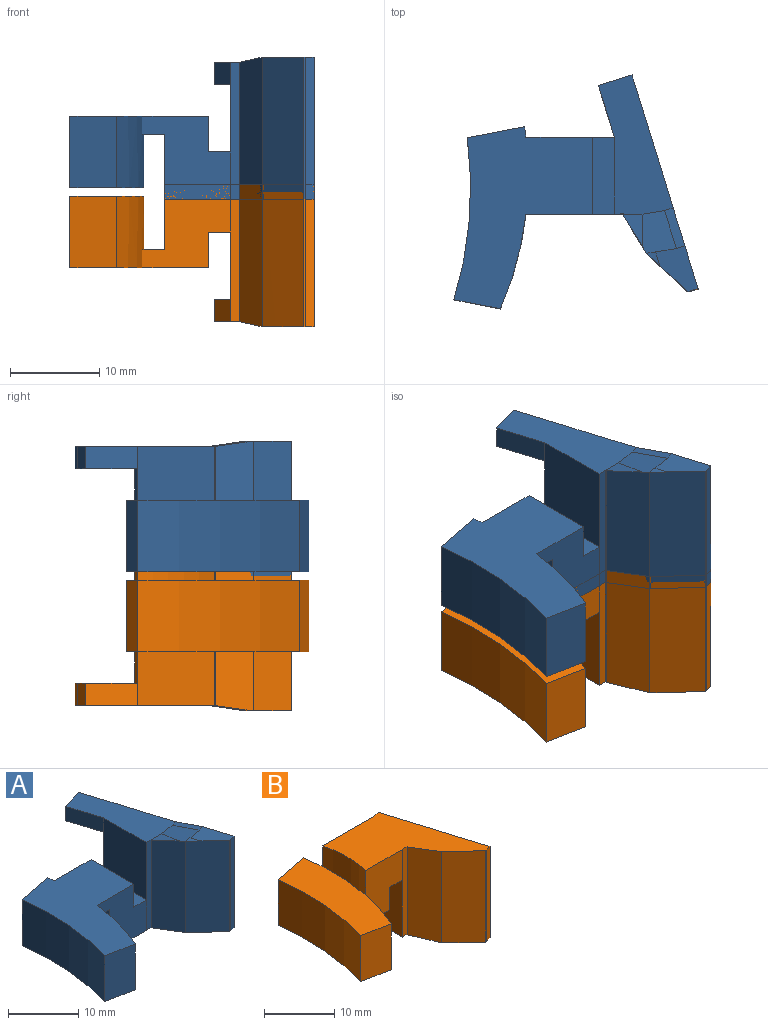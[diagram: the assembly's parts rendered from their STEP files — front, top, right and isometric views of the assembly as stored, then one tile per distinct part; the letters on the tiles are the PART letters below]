
ASSEMBLY  parts=2 mates=1
PART A: 36 faces, bbox 27.3x26.1x15.9 mm
  f0: plane 15.92x4.24mm, normal (0.96,0.3,0), area 69.4mm2, adj f4,f20,f29,f30
  f1: plane 15.32x0.16mm, normal (-0.99,0.14,0), area 2.5mm2, adj f6,f20,f24,f27,f33
  f2: plane 15.92x0mm, normal (-0.96,-0.29,0), area 0mm2, adj f6,f7,f20
  f3: plane 15.92x0.2mm, normal (0.16,-0.99,0), area 3.2mm2, adj f5,f7,f20,f35
  f4: plane 15.92x4.78mm, normal (0.96,0.29,0), area 79.6mm2, adj f0,f5,f20,f35
  f5: plane 15.92x0.96mm, normal (0.29,-0.96,0), area 15.9mm2, adj f3,f4,f20,f35
  f6: plane 15.92x4.25mm, normal (-0.85,-0.52,0), area 77.8mm2, adj f1,f2,f20,f26,f27
  f7: plane 15.92x4.6mm, normal (-0.68,-0.73,0), area 99.9mm2, adj f2,f3,f20,f34,f35
  f8: plane 5.81x2.5mm, normal (-0.96,-0.3,0), area 15.2mm2, adj f22,f24,f25,f32
  f9: plane 6.67x2.5mm, normal (0.96,0.3,0), area 17.5mm2, adj f24,f25,f29,f31
  f10: plane 9.9x9.3mm, normal (0,-1,0), area 63.8mm2, adj f11,f15,f18,f19,f20,f21,f23,f33
  f11: plane 20.36x15.45mm, normal (0,0,1), area 181.4mm2, adj f10,f12,f13,f14,f15,f16,f21
  f12: plane 12.97x12.8mm, normal (0,1,0), area 103.1mm2, adj f11,f15,f18,f19,f20,f21,f22,f23
  f13: cylinder r=42.23mm len=18.11mm, axis (0,0,-1), area 146.5mm2, adj f11,f14,f16,f17
  f14: plane 8x5.2mm, normal (-0.19,-0.98,0), area 42.4mm2, adj f11,f13,f15,f17
  f15: cylinder r=37.1mm len=20.36mm, axis (0,0,-1), area 149.3mm2, adj f10,f11,f12,f14,f16,f17,f18
  f16: plane 8x6.4mm, normal (-0.19,0.98,0), area 52.2mm2, adj f11,f13,f15,f17
  f17: plane 20.36x8.31mm, normal (0,0,-1), area 119.3mm2, adj f13,f14,f15,f16
  f18: plane 8.6x3.05mm, normal (0,0,-1), area 23.2mm2, adj f10,f12,f15,f19
  f19: cylinder r=17.21mm len=8.6mm, axis (0,0,1), area 63.5mm2, adj f10,f12,f18,f20
  f20: plane 17.54x16.74mm, normal (0,0,-1), area 142.3mm2, adj f0,f1,f2,f3,f4,f5,f6,f7
  f21: plane 8.6x4mm, normal (1,0,0), area 34.4mm2, adj f10,f11,f12,f23
  f22: plane 10x8.6mm, normal (-1,0,0), area 86mm2, adj f8,f12,f23,f24,f33
  f23: plane 8.6x2.5mm, normal (0,0,1), area 21.5mm2, adj f10,f12,f21,f22
  f24: plane 15.57x8.35mm, normal (0,0,1), area 72mm2, adj f1,f8,f9,f22,f26,f27,f29,f30
  f25: plane 6.97x5.83mm, normal (0,0,-1), area 26.2mm2, adj f8,f9,f12,f28,f31,f32
  f26: plane 4.79x3.85mm, normal (-0.02,0.14,0.99), area 14mm2, adj f6,f24,f27,f30,f34,f35
  f27: plane 3.66x2.17mm, normal (0,0.14,0.99), area 4mm2, adj f1,f6,f24,f26
  f28: plane 12.8x0.96mm, normal (-0.29,0.96,0), area 12.8mm2, adj f12,f20,f25,f29
  f29: plane 15.3x8.19mm, normal (0.96,0.29,0), area 131.1mm2, adj f0,f9,f20,f24,f28
  f30: plane 4.54x2.27mm, normal (-0.04,0.13,0.99), area 4.5mm2, adj f0,f24,f26,f35
  f31: plane 2.5x0.96mm, normal (-0.29,0.96,0), area 2.5mm2, adj f9,f24,f25,f32
  f32: plane 2.81x2.5mm, normal (-0.3,0.96,0), area 7.3mm2, adj f8,f24,f25,f31
  f33: plane 15.3x1.02mm, normal (0.03,-1,0), area 15.5mm2, adj f1,f10,f20,f22,f24
  f34: plane 1.53x1.47mm, normal (0,0,1), area 0.8mm2, adj f7,f26,f35
  f35: plane 5.1x4.75mm, normal (0,0,1), area 13mm2, adj f3,f4,f5,f7,f26,f30,f34
PART B: 36 faces, bbox 27.3x26.1x15.9 mm
  f0: plane 15.92x4.24mm, normal (0.96,0.3,0), area 69.4mm2, adj f4,f20,f29,f30
  f1: plane 15.32x0.16mm, normal (-0.99,0.14,0), area 2.5mm2, adj f6,f20,f24,f27,f33
  f2: plane 15.92x0mm, normal (-0.96,-0.29,0), area 0mm2, adj f6,f7,f20
  f3: plane 15.92x0.2mm, normal (0.16,-0.99,0), area 3.2mm2, adj f5,f7,f20,f35
  f4: plane 15.92x4.78mm, normal (0.96,0.29,0), area 79.6mm2, adj f0,f5,f20,f35
  f5: plane 15.92x0.96mm, normal (0.29,-0.96,0), area 15.9mm2, adj f3,f4,f20,f35
  f6: plane 15.92x4.25mm, normal (-0.85,-0.52,0), area 77.8mm2, adj f1,f2,f20,f26,f27
  f7: plane 15.92x4.6mm, normal (-0.68,-0.73,0), area 99.9mm2, adj f2,f3,f20,f34,f35
  f8: plane 5.81x2.5mm, normal (-0.96,-0.3,0), area 15.2mm2, adj f22,f24,f25,f32
  f9: plane 6.67x2.5mm, normal (0.96,0.3,0), area 17.5mm2, adj f24,f25,f29,f31
  f10: plane 9.9x9.3mm, normal (0,-1,0), area 63.8mm2, adj f11,f15,f18,f19,f20,f21,f23,f33
  f11: plane 20.36x15.45mm, normal (0,0,-1), area 181.4mm2, adj f10,f12,f13,f14,f15,f16,f21
  f12: plane 12.97x12.8mm, normal (0,1,0), area 103.1mm2, adj f11,f15,f18,f19,f20,f21,f22,f23
  f13: cylinder r=42.23mm len=18.11mm, axis (0,0,1), area 146.5mm2, adj f11,f14,f16,f17
  f14: plane 8x5.2mm, normal (-0.19,-0.98,0), area 42.4mm2, adj f11,f13,f15,f17
  f15: cylinder r=37.1mm len=20.36mm, axis (0,0,1), area 149.3mm2, adj f10,f11,f12,f14,f16,f17,f18
  f16: plane 8x6.4mm, normal (-0.19,0.98,0), area 52.2mm2, adj f11,f13,f15,f17
  f17: plane 20.36x8.31mm, normal (0,0,1), area 119.3mm2, adj f13,f14,f15,f16
  f18: plane 8.6x3.05mm, normal (0,0,1), area 23.2mm2, adj f10,f12,f15,f19
  f19: cylinder r=17.21mm len=8.6mm, axis (0,0,-1), area 63.5mm2, adj f10,f12,f18,f20
  f20: plane 17.54x16.74mm, normal (0,0,1), area 142.3mm2, adj f0,f1,f2,f3,f4,f5,f6,f7
  f21: plane 8.6x4mm, normal (1,0,0), area 34.4mm2, adj f10,f11,f12,f23
  f22: plane 10x8.6mm, normal (-1,0,0), area 86mm2, adj f8,f12,f23,f24,f33
  f23: plane 8.6x2.5mm, normal (0,0,-1), area 21.5mm2, adj f10,f12,f21,f22
  f24: plane 15.57x8.35mm, normal (0,0,-1), area 72mm2, adj f1,f8,f9,f22,f26,f27,f29,f30
  f25: plane 6.97x5.83mm, normal (0,0,1), area 26.2mm2, adj f8,f9,f12,f28,f31,f32
  f26: plane 4.79x3.85mm, normal (-0.02,0.14,-0.99), area 14mm2, adj f6,f24,f27,f30,f34,f35
  f27: plane 3.66x2.17mm, normal (0,0.14,-0.99), area 4mm2, adj f1,f6,f24,f26
  f28: plane 12.8x0.96mm, normal (-0.29,0.96,0), area 12.8mm2, adj f12,f20,f25,f29
  f29: plane 15.3x8.19mm, normal (0.96,0.29,0), area 131.1mm2, adj f0,f9,f20,f24,f28
  f30: plane 4.54x2.27mm, normal (-0.04,0.13,-0.99), area 4.5mm2, adj f0,f24,f26,f35
  f31: plane 2.5x0.96mm, normal (-0.29,0.96,0), area 2.5mm2, adj f9,f24,f25,f32
  f32: plane 2.81x2.5mm, normal (-0.3,0.96,0), area 7.3mm2, adj f8,f24,f25,f31
  f33: plane 15.3x1.02mm, normal (0.03,-1,0), area 15.5mm2, adj f1,f10,f20,f22,f24
  f34: plane 1.53x1.47mm, normal (0,0,-1), area 0.8mm2, adj f7,f26,f35
  f35: plane 5.1x4.75mm, normal (0,0,-1), area 13mm2, adj f3,f4,f5,f7,f26,f30,f34
PLACE A t=(5.85,-4.14,-48.66)mm
PLACE B t=(5.85,-4.14,-47.01)mm
MATE parallel A.f20 <-> B.f20  axis (0,0,-1) through (9.37,-1.84,-47.84)mm
